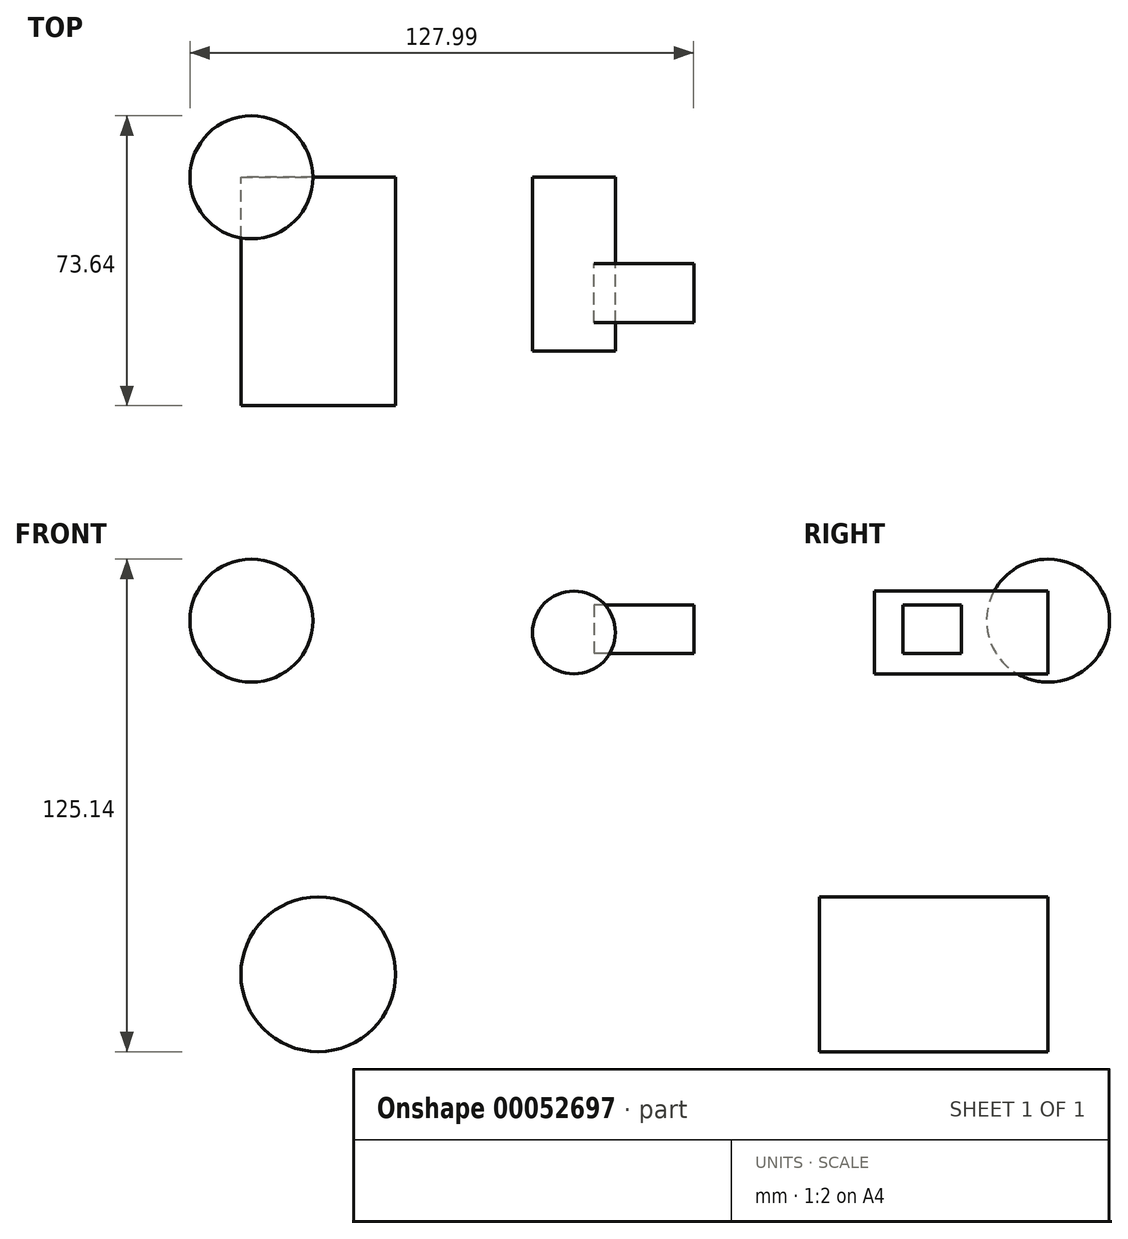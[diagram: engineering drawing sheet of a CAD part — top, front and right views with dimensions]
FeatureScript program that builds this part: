
annotation { "Feature Type Name" : "Feature", "Feature Type Description" : "" }
export const myFeature = defineFeature(function(context is Context, id is Id, definition is map)
    precondition{}
    {
        {
            var Q0;
            Q0=qCreatedBy(makeId("Front.planeOp"),FACE);
            var sketch = newSketch(context, id + "F0", { "sketchPlane" : qUnion([Q0])});
            skCircle(sketch, "E0", {"center": v(-50.17, 47.9) * mm, "radius": 15.63 * mm});
            skLineSegment(sketch, "E1", {"start": v(-50.17, 63.53) * mm, "end": v(-50.17, 32.28) * mm});
            skSolve(sketch);
        }
        {
            var Q0;
            {var subQ0=sQuery(id+"F0.wireOp",EDGE,"E1");Q0=makeQuery(id+"F0.imprint","IMPRINT",FACE,{"disambiguationData":[TD([[makeQuery(id+"F0.imprint","IMPRINT",EDGE,{"derivedFrom":subQ0}),1.0]])]});}
            var Q1;
            Q1=sQuery(id+"F0.wireOp",EDGE,"E1");
            revolve(context, id + "F1", {"entities" : qUnion([Q0]), "axis" : qUnion([Q1]), "revolveType" : RevolveType.FULL});
        }
        {
            var Q0;
            Q0=qCreatedBy(makeId("Front.planeOp"),FACE);
            var sketch = newSketch(context, id + "F2", { "sketchPlane" : qUnion([Q0])});
            skCircle(sketch, "E2", {"center": v(31.77, 44.9) * mm, "radius": 10.52 * mm});
            skCircle(sketch, "E3", {"center": v(-39.03, -42.45) * mm, "radius": 20.32 * mm});
            skSolve(sketch);
        }
        {
            var Q0;
            Q0=makeQuery(id+"F2.imprint","IMPRINT",FACE,{"disambiguationData":[TD([[makeQuery(id+"F2.imprint","IMPRINT",EDGE,{"derivedFrom":sQuery(id+"F2.wireOp",EDGE,"E2")}),1.0]])]});
            extrude(context, id + "F3", {"entities" : qUnion([Q0]), "depth" : 44.1 * mm});
        }
        {
            var Q0;
            Q0=qCreatedBy(makeId("Front.planeOp"),FACE);
            var sketch = newSketch(context, id + "F4", { "sketchPlane" : qUnion([Q0])});
            skCircle(sketch, "E4", {"center": v(-33.2, -41.96) * mm, "radius": 19.66 * mm});
            skSolve(sketch);
        }
        {
            var Q0;
            Q0=makeQuery(id+"F4.imprint","IMPRINT",FACE,{"disambiguationData":[TD([[makeQuery(id+"F4.imprint","IMPRINT",EDGE,{"derivedFrom":sQuery(id+"F4.wireOp",EDGE,"E4")}),1.0]])]});
            extrude(context, id + "F5", {"entities" : qUnion([Q0]), "depth" : 58 * mm});
        }
        {
            var Q0;
            Q0=qCreatedBy(makeId("Right.planeOp"),FACE);
            var sketch = newSketch(context, id + "F6", { "sketchPlane" : qUnion([Q0])});
            skLineSegment(sketch, "E5.bottom", {"start": v(-59.47, 49.83) * mm, "end": v(-44.56, 49.83) * mm});
            skLineSegment(sketch, "E5.top", {"start": v(-59.47, 37.59) * mm, "end": v(-44.56, 37.59) * mm});
            skLineSegment(sketch, "E5.left", {"start": v(-59.47, 49.83) * mm, "end": v(-59.47, 37.59) * mm});
            skLineSegment(sketch, "E5.right", {"start": v(-44.56, 49.83) * mm, "end": v(-44.56, 37.59) * mm});
            skSolve(sketch);
        }
        {
            var Q0;
            Q0=makeQuery(id+"F6.imprint","IMPRINT",FACE,{"disambiguationData":[TD([[makeQuery(id+"F6.imprint","IMPRINT",EDGE,{"derivedFrom":sQuery(id+"F6.wireOp",EDGE,"E5.bottom")}),-1.0]])]});
            extrude(context, id + "F7", {"entities" : qUnion([Q0]), "depth" : 25.4 * mm});
        }
        {
            var Q0;
            Q0=makeQuery(id+"F7.opExtrude","SWEPT_BODY",BODY,{"disambiguationData":[OSD([sQuery(id+"F6.wireOp",EDGE,"E5.bottom"),sQuery(id+"F6.wireOp",EDGE,"E5.top"),sQuery(id+"F6.wireOp",EDGE,"E5.left"),sQuery(id+"F6.wireOp",EDGE,"E5.right")])]});
            transform(context, id + "F8", {"entities" : qUnion([Q0]), "transformType" : TransformType.TRANSLATION_3D, "dx" : 36.8 * mm, "dy" : 22.57 * mm, "dz" : 2 * mm, "makeCopy" : false});
        }
    });
